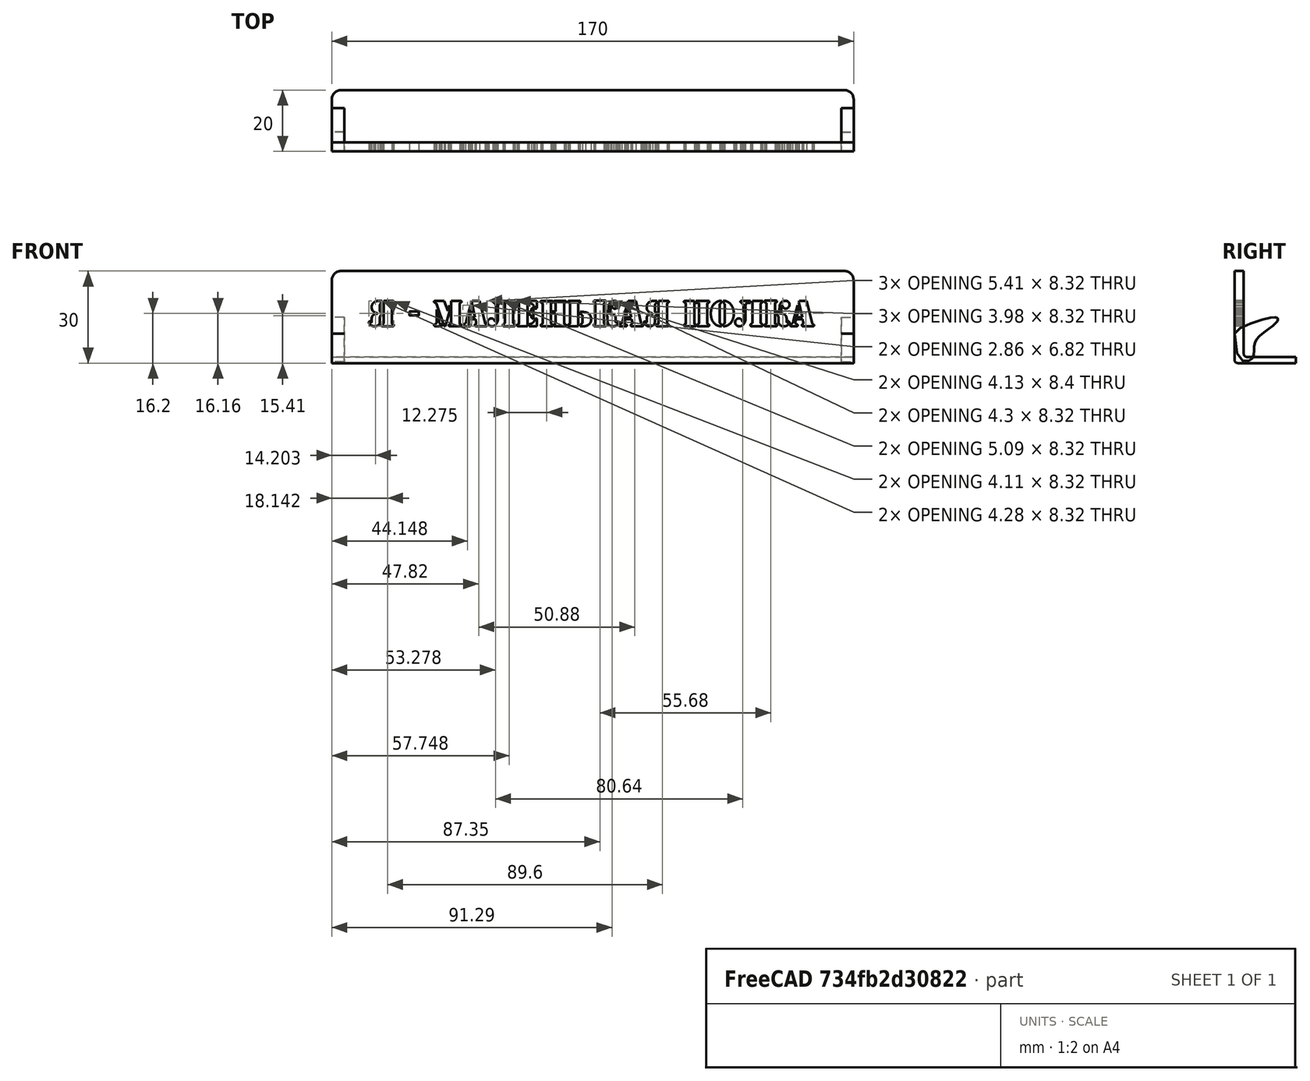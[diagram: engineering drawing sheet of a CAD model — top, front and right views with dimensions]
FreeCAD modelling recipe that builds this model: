
FCSTD DOCUMENT  (FreeCAD 0.18.4R)
Label: power_point_shelf
License: All rights reserved
LicenseURL: http://en.wikipedia.org/wiki/All_rights_reserved
objects: Part::Box×2, Part::MultiFuse×1, Part::Fillet×1, Sketcher::SketchObject×1, PartDesign::Pad×1, PartDesign::Body×1, Part::Mirroring×1, Part::Compound×1, App::Part×1, Part::Part2DObjectPython×1, Part::Extrusion×1, Part::Cut×1
note: 13 computed .brp shape members not serialized (recipe doc carries the construction recipe); baked Part::Feature solids carry a one-line shape summary decoded from their .brp

FEATURE [Part::Box] Box  label="Cube"
  AttacherType = Attacher::AttachEngine3D
  Height = 2
  Length = 170
  Width = 20
FEATURE [Part::Box] Box001  label="Cube001"
  AttacherType = Attacher::AttachEngine3D
  Height = 30
  Length = 170
  Width = 3
FEATURE [Part::MultiFuse] Fusion
  Shapes = -> [Box,Box001]
FEATURE [Part::Fillet] Fillet  label="power point shelf fillet"
  Base = -> Fusion
  Edges = 6 edges: [Edge5 r=1,Edge9 r=3,Edge12 r=3,Edge21 r=3,Edge23 r=1,Edge27 r=3]
FEATURE [Sketcher::SketchObject] Sketch
  MapMode = 5
  Placement = pos=(0,0,0) rot=(0.57735,0.57735,0.57735;2.0944rad)
  Support = -> [YZ_Plane001]
  sketch-geometry (19):
    g0-g9: Circle [constr] x10 (B-spline internal-alignment scaffolding for g10; pole/knot coordinates omitted)
    g10: BSplineCurve PolesCount=10 KnotsCount=8 Degree=3 IsPeriodic=0
    g11-g18: GeomPoint [constr] x8 (B-spline internal-alignment scaffolding for g10; pole/knot coordinates omitted)
  constraints (10):
    c: Radius(g0) = 0.3
    c: Equal(g0, g1-g7) x7
    c: PointOnObject(g7,g-1)
    c: Equal(g0,g8)
    c: Coincident(g8,g-1)
    c: Equal(g0,g9)
    c: InternalAlignment(g0-g9 -> g10) x10
    c: InternalAlignment(g11-g18 -> g10) x8
    c: PointOnObject(g10,g-2)
    c: Coincident(g10,g10)
FEATURE [PartDesign::Pad] Pad
  Length = 4
  Length2 = 100
  Placement = pos=(0,0,0) rot=(0.57735,0.57735,0.57735;2.0944rad)
  Profile = -> Sketch
  Type = 0
FEATURE [PartDesign::Body] Body
  Group = -> [Sketch,Pad]
  Origin = -> Origin001
  Tip = -> Pad
FEATURE [Part::Mirroring] Part__Mirroring  label="Body (Mirror #1)"
  Base = (85,0,0)
  Normal = (1,0,0)
  Source = -> Body
FEATURE [Part::Compound] Compound  label="power point shelf compound"
  Links = -> [Body,Part__Mirroring,Fillet]
FEATURE [App::Part] Part  label="power point shelf part"
  Group = -> [Fusion,Box,Box001,Fillet,Body,Part__Mirroring,Compound]
  Origin = -> Origin
FEATURE [Part::Part2DObjectPython] ShapeString  # Draft 2D object (typed FeaturePython)
  FontFile = <userpath>/install/fonts/stencil_[allfont.net].ttf
  Placement = pos=(12,10,12) rot=(1,0,0;1.5708rad)
  Size = 5
  String = Я - МАЛЕНЬКАЯ ПОЛКА
  Tracking = 0
FEATURE [Part::Extrusion] Extrude
  Base = -> ShapeString
  Dir = (0,-1,2e-16)
  DirMode = 2
  FaceMakerClass = Part::FaceMakerBullseye
  LengthFwd = 10
  LengthRev = 0
  Solid = false
  Symmetric = false
FEATURE [Part::Cut] Cut
  Base = -> Fillet
  Tool = -> Extrude
